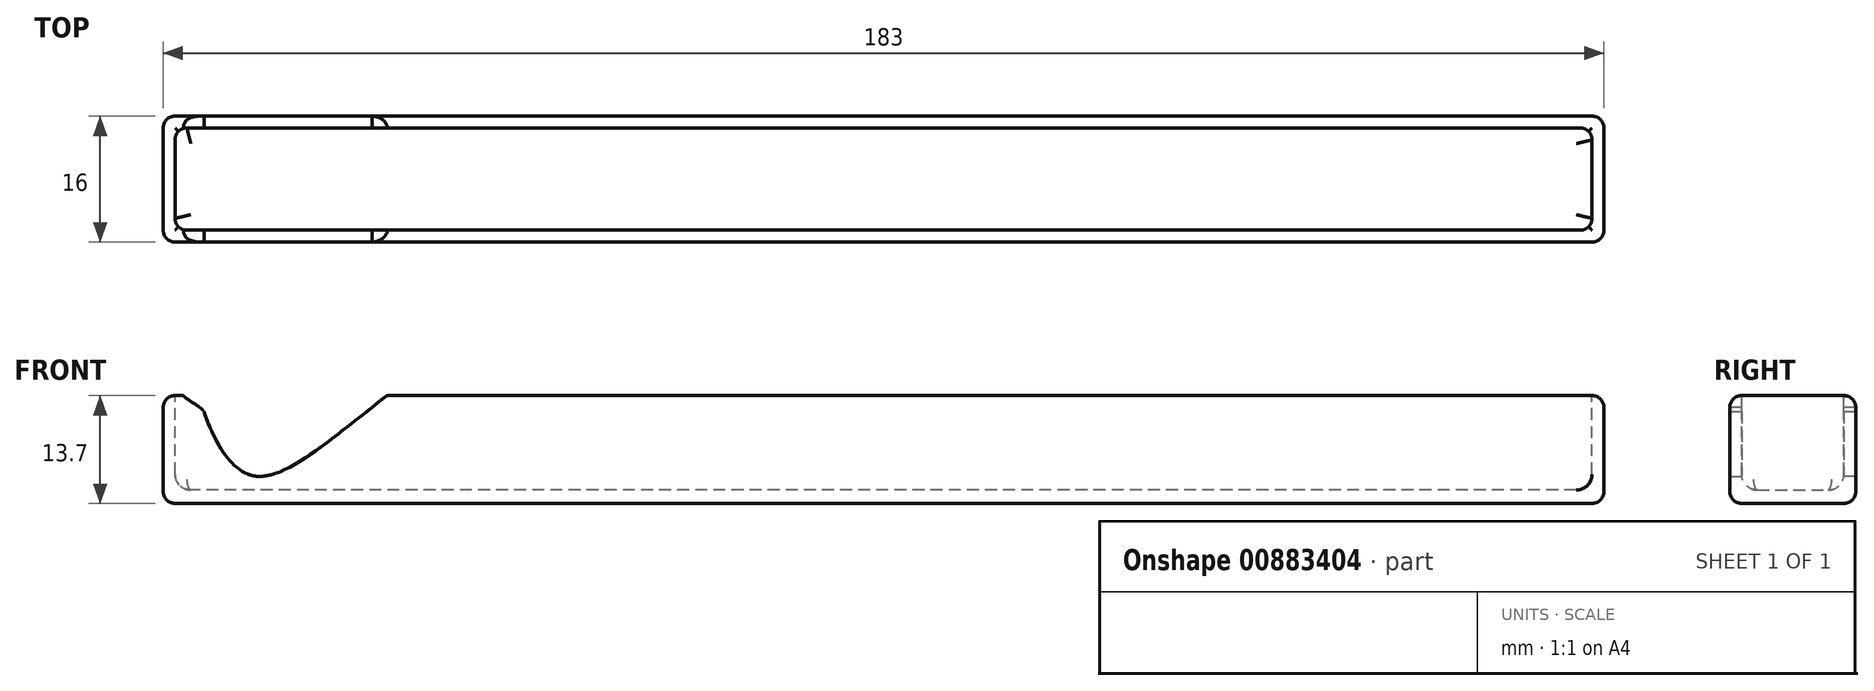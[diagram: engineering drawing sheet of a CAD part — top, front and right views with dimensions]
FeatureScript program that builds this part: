
annotation { "Feature Type Name" : "Feature", "Feature Type Description" : "" }
export const myFeature = defineFeature(function(context is Context, id is Id, definition is map)
    precondition{}
    {
        {
            var Q0;
            Q0=qCreatedBy(makeId("Top.planeOp"),FACE);
            var sketch = newSketch(context, id + "F0", { "sketchPlane" : qUnion([Q0])});
            skLineSegment(sketch, "E0.bottom", {"start": v(91.5, 8) * mm, "end": v(-91.5, 8) * mm});
            skLineSegment(sketch, "E0.top", {"start": v(91.5, -8) * mm, "end": v(-91.5, -8) * mm});
            skLineSegment(sketch, "E0.left", {"start": v(91.5, 8) * mm, "end": v(91.5, -8) * mm});
            skLineSegment(sketch, "E0.right", {"start": v(-91.5, 8) * mm, "end": v(-91.5, -8) * mm});
            skPoint(sketch, "E0.middle", {"position": v(0, 0) * mm});
            skSolve(sketch);
        }
        {
            var Q0;
            Q0=makeQuery(id+"F0.imprint","IMPRINT",FACE,{"disambiguationData":[TD([[makeQuery(id+"F0.imprint","IMPRINT",EDGE,{"derivedFrom":sQuery(id+"F0.wireOp",EDGE,"E0.bottom")}),1.0]])]});
            extrude(context, id + "F1", {"entities" : qUnion([Q0]), "depth" : 13.7 * mm, "offsetDistance" : 25 * mm});
        }
        {
            var Q0;
            Q0=makeQuery(id+"F1.opExtrude","CAP_FACE",FACE,{"disambiguationData":[OSD([sQuery(id+"F0.wireOp",EDGE,"E0.bottom"),sQuery(id+"F0.wireOp",EDGE,"E0.top"),sQuery(id+"F0.wireOp",EDGE,"E0.left"),sQuery(id+"F0.wireOp",EDGE,"E0.right")])],"isStart":false});
            var sketch = newSketch(context, id + "F2", { "sketchPlane" : qUnion([Q0])});
            skLineSegment(sketch, "E1.bottom", {"start": v(90, -6.5) * mm, "end": v(-90, -6.5) * mm});
            skLineSegment(sketch, "E1.top", {"start": v(90, 6.5) * mm, "end": v(-90, 6.5) * mm});
            skLineSegment(sketch, "E1.left", {"start": v(90, -6.5) * mm, "end": v(90, 6.5) * mm});
            skLineSegment(sketch, "E1.right", {"start": v(-90, -6.5) * mm, "end": v(-90, 6.5) * mm});
            skPoint(sketch, "E1.middle", {"position": v(0, 0) * mm});
            skSolve(sketch);
        }
        {
            var Q0;
            Q0=makeQuery(id+"F2.imprint","IMPRINT",FACE,{"disambiguationData":[TD([[makeQuery(id+"F2.imprint","IMPRINT",EDGE,{"derivedFrom":sQuery(id+"F2.wireOp",EDGE,"E1.bottom")}),-1.0]])]});
            extrude(context, id + "F3", {"entities" : qUnion([Q0]), "operationType" : NewBodyOperationType.REMOVE, "oppositeDirection" : true, "depth" : 12 * mm, "offsetDistance" : 25 * mm});
        }
        {
            var Q0;
            Q0=makeQuery(id+"F3.boolean.opBoolean","COPY",EDGE,{"derivedFrom":makeQuery(id+"F3.opExtrude","CAP_EDGE",EDGE,{"disambiguationData":[OSD([sQuery(id+"F2.wireOp",EDGE,"E1.top")])],"isStart":false})});
            var Q1;
            Q1=makeQuery(id+"F3.boolean.opBoolean","COPY",EDGE,{"derivedFrom":makeQuery(id+"F3.opExtrude","CAP_EDGE",EDGE,{"disambiguationData":[OSD([sQuery(id+"F2.wireOp",EDGE,"E1.bottom")])],"isStart":false})});
            var Q2;
            Q2=makeQuery(id+"F3.boolean.opBoolean","COPY",EDGE,{"derivedFrom":makeQuery(id+"F3.opExtrude","CAP_EDGE",EDGE,{"disambiguationData":[OSD([sQuery(id+"F2.wireOp",EDGE,"E1.left")])],"isStart":false})});
            var Q3;
            Q3=makeQuery(id+"F3.boolean.opBoolean","COPY",EDGE,{"derivedFrom":makeQuery(id+"F3.opExtrude","CAP_EDGE",EDGE,{"disambiguationData":[OSD([sQuery(id+"F2.wireOp",EDGE,"E1.right")])],"isStart":false})});
            fillet(context, id + "F4", {"entities" : qUnion([Q0, Q1, Q2, Q3]), "radius" : 2 * mm, "tangentPropagation" : true, "allowEdgeOverflow" : false});
        }
        {
            var Q0;
            Q0=makeQuery(id+"F1.opExtrude","CAP_EDGE",EDGE,{"disambiguationData":[OSD([sQuery(id+"F0.wireOp",EDGE,"E0.top")])],"isStart":true});
            var Q1;
            Q1=makeQuery(id+"F1.opExtrude","SWEPT_EDGE",EDGE,{"disambiguationData":[OSD([sQuery(id+"F0.wireOp",EDGE,"E0.top"),sQuery(id+"F0.wireOp",EDGE,"E0.right")])]});
            var Q2;
            Q2=makeQuery(id+"F1.opExtrude","SWEPT_EDGE",EDGE,{"disambiguationData":[OSD([sQuery(id+"F0.wireOp",EDGE,"E0.bottom"),sQuery(id+"F0.wireOp",EDGE,"E0.right")])]});
            var Q3;
            Q3=makeQuery(id+"F1.opExtrude","CAP_EDGE",EDGE,{"disambiguationData":[OSD([sQuery(id+"F0.wireOp",EDGE,"E0.right")])],"isStart":true});
            var Q4;
            Q4=makeQuery(id+"F1.opExtrude","CAP_EDGE",EDGE,{"disambiguationData":[OSD([sQuery(id+"F0.wireOp",EDGE,"E0.bottom")])],"isStart":true});
            var Q5;
            Q5=makeQuery(id+"F1.opExtrude","SWEPT_EDGE",EDGE,{"disambiguationData":[OSD([sQuery(id+"F0.wireOp",EDGE,"E0.bottom"),sQuery(id+"F0.wireOp",EDGE,"E0.left")])]});
            var Q6;
            Q6=makeQuery(id+"F1.opExtrude","CAP_EDGE",EDGE,{"disambiguationData":[OSD([sQuery(id+"F0.wireOp",EDGE,"E0.left")])],"isStart":true});
            var Q7;
            Q7=makeQuery(id+"F1.opExtrude","SWEPT_EDGE",EDGE,{"disambiguationData":[OSD([sQuery(id+"F0.wireOp",EDGE,"E0.top"),sQuery(id+"F0.wireOp",EDGE,"E0.left")])]});
            var Q8;
            Q8=makeQuery(id+"F1.opExtrude","CAP_EDGE",EDGE,{"disambiguationData":[OSD([sQuery(id+"F0.wireOp",EDGE,"E0.top")])],"isStart":false});
            var Q9;
            Q9=makeQuery(id+"F1.opExtrude","CAP_EDGE",EDGE,{"disambiguationData":[OSD([sQuery(id+"F0.wireOp",EDGE,"E0.right")])],"isStart":false});
            var Q10;
            Q10=makeQuery(id+"F1.opExtrude","CAP_EDGE",EDGE,{"disambiguationData":[OSD([sQuery(id+"F0.wireOp",EDGE,"E0.bottom")])],"isStart":false});
            var Q11;
            Q11=makeQuery(id+"F1.opExtrude","CAP_EDGE",EDGE,{"disambiguationData":[OSD([sQuery(id+"F0.wireOp",EDGE,"E0.left")])],"isStart":false});
            fillet(context, id + "F5", {"entities" : qUnion([Q0, Q1, Q2, Q3, Q4, Q5, Q6, Q7, Q8, Q9, Q10, Q11]), "radius" : 1.5 * mm, "tangentPropagation" : true, "allowEdgeOverflow" : false});
        }
        {
            var Q0;
            Q0=makeQuery(id+"F3.boolean.opBoolean","COPY",EDGE,{"derivedFrom":makeQuery(id+"F3.opExtrude","SWEPT_EDGE",EDGE,{"disambiguationData":[OSD([sQuery(id+"F2.wireOp",EDGE,"E1.top"),sQuery(id+"F2.wireOp",EDGE,"E1.left")])]})});
            var Q1;
            Q1=makeQuery(id+"F3.boolean.opBoolean","COPY",EDGE,{"derivedFrom":makeQuery(id+"F3.opExtrude","SWEPT_EDGE",EDGE,{"disambiguationData":[OSD([sQuery(id+"F2.wireOp",EDGE,"E1.bottom"),sQuery(id+"F2.wireOp",EDGE,"E1.left")])]})});
            var Q2;
            Q2=makeQuery(id+"F3.boolean.opBoolean","COPY",EDGE,{"derivedFrom":makeQuery(id+"F3.opExtrude","SWEPT_EDGE",EDGE,{"disambiguationData":[OSD([sQuery(id+"F2.wireOp",EDGE,"E1.bottom"),sQuery(id+"F2.wireOp",EDGE,"E1.right")])]})});
            var Q3;
            Q3=makeQuery(id+"F3.boolean.opBoolean","COPY",EDGE,{"derivedFrom":makeQuery(id+"F3.opExtrude","SWEPT_EDGE",EDGE,{"disambiguationData":[OSD([sQuery(id+"F2.wireOp",EDGE,"E1.top"),sQuery(id+"F2.wireOp",EDGE,"E1.right")])]})});
            fillet(context, id + "F6", {"entities" : qUnion([Q0, Q1, Q2, Q3]), "radius" : 1.5 * mm, "tangentPropagation" : true, "allowEdgeOverflow" : false});
        }
        {
            var Q0;
            Q0=makeQuery(id+"F1.opExtrude","SWEPT_FACE",FACE,{"disambiguationData":[OSD([sQuery(id+"F0.wireOp",EDGE,"E0.top")])]});
            var sketch = newSketch(context, id + "F7", { "sketchPlane" : qUnion([Q0])});
            skLineSegment(sketch, "E2", {"start": v(-90, 1.5) * mm, "end": v(-80, 1.5) * mm});
            skLineSegment(sketch, "E3", {"start": v(-86.33, 14.17) * mm, "end": v(-64.87, 14.17) * mm});
            skLineSegment(sketch, "E4", {"start": v(-64.87, 14.17) * mm, "end": v(-61.7, 14.17) * mm});
            skPoint(sketch, "E5.2.internal.snap0", {"position": v(-86.33, 12.9) * mm});
            skFitSpline(sketch, "E5", {"points": [v(-86.33, 11.63) * mm, v(-88.56, 14.19) * mm, v(-86.33, 14.56) * mm], "startDerivative": vector(-1.87, 4.67) * mm, "endDerivative": vector(-25.77, 2.55) * mm});
            skLineSegment(sketch, "E6", {"start": v(-86.33, 14.17) * mm, "end": v(-88.61, 14.17) * mm});
            skLineSegment(sketch, "E7", {"start": v(-80, 1.5) * mm, "end": v(-80, 3.5) * mm});
            skFitSpline(sketch, "E8", {"points": [v(-86.33, 11.63) * mm, v(-80, 3.5) * mm, v(-64.94, 12.2) * mm], "startDerivative": vector(9.18, -25.39) * mm, "endDerivative": vector(30.33, 23.04) * mm});
            skFitSpline(sketch, "E9", {"points": [v(-64.94, 12.2) * mm, v(-61.7, 14.17) * mm, v(-59.18, 12.9) * mm], "startDerivative": vector(6.18, 5.4) * mm, "endDerivative": vector(5.32, -4.22) * mm});
            skSolve(sketch);
        }
        {
            var Q0;
            Q0 = qSketchRegion(id + "F7", true);
            extrude(context, id + "F8", {"entities" : qUnion([Q0]), "operationType" : NewBodyOperationType.REMOVE, "oppositeDirection" : true, "depth" : 25 * mm, "offsetDistance" : 25 * mm});
        }
    });
